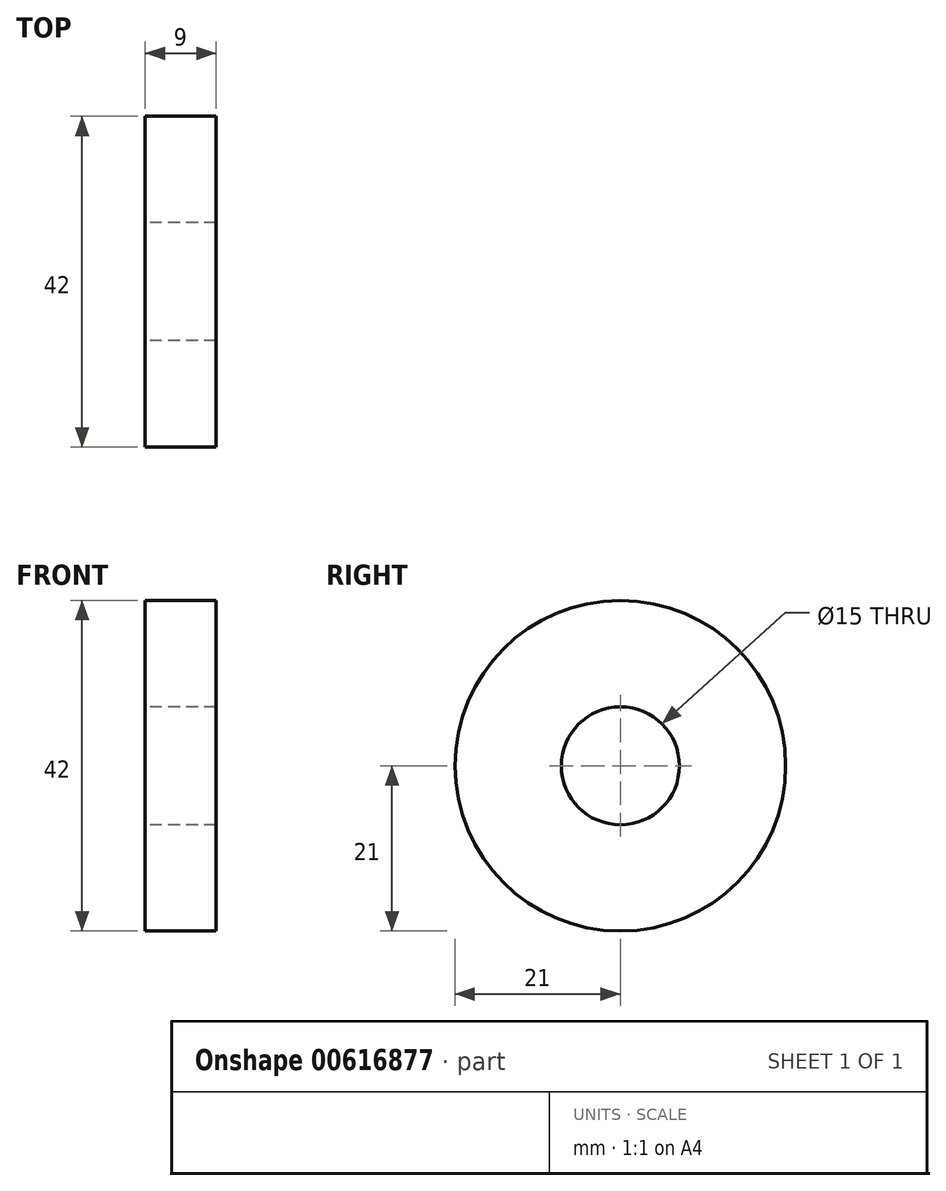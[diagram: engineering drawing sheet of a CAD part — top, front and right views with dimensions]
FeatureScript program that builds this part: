
annotation { "Feature Type Name" : "Feature", "Feature Type Description" : "" }
export const myFeature = defineFeature(function(context is Context, id is Id, definition is map)
    precondition{}
    {
        {
            var Q0;
            Q0=qCreatedBy(makeId("Right.planeOp"),FACE);
            var sketch = newSketch(context, id + "F0", { "sketchPlane" : qUnion([Q0])});
            skCircle(sketch, "E0", {"center": v(0, 0) * mm, "radius": 7.5 * mm});
            skCircle(sketch, "E1", {"center": v(0, 0) * mm, "radius": 21 * mm});
            skSolve(sketch);
        }
        {
            var Q0;
            Q0=makeQuery(id+"F0.imprint","IMPRINT",FACE,{"disambiguationData":[TD([[makeQuery(id+"F0.imprint","IMPRINT",EDGE,{"derivedFrom":sQuery(id+"F0.wireOp",EDGE,"E0")}),-1.0]])]});
            extrude(context, id + "F1", {"entities" : qUnion([Q0]), "depth" : 9 * mm, "offsetDistance" : 25 * mm});
        }
    });
